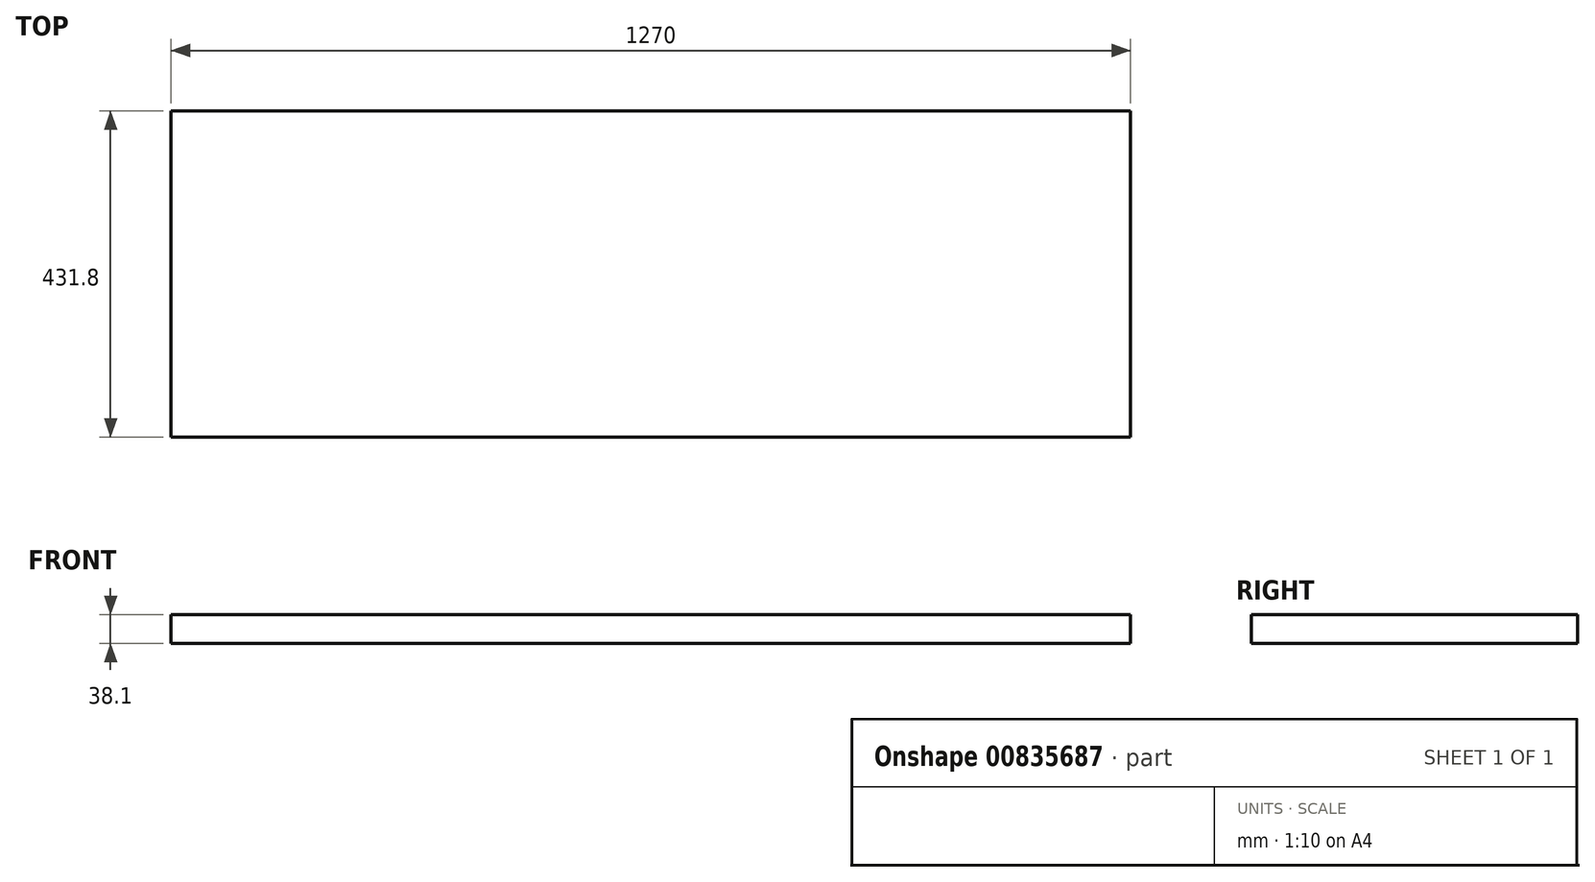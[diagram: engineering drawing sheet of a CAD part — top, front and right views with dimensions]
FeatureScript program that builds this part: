
annotation { "Feature Type Name" : "Feature", "Feature Type Description" : "" }
export const myFeature = defineFeature(function(context is Context, id is Id, definition is map)
    precondition{}
    {
        {
            var Q0;
            Q0=qCreatedBy(makeId("Top.planeOp"),FACE);
            var sketch = newSketch(context, id + "F0", { "sketchPlane" : qUnion([Q0])});
            skLineSegment(sketch, "E0.bottom", {"start": v(0, 0) * mm, "end": v(1270, 0) * mm});
            skLineSegment(sketch, "E0.top", {"start": v(0, -431.8) * mm, "end": v(1270, -431.8) * mm});
            skLineSegment(sketch, "E0.left", {"start": v(0, 0) * mm, "end": v(0, -431.8) * mm});
            skLineSegment(sketch, "E0.right", {"start": v(1270, 0) * mm, "end": v(1270, -431.8) * mm});
            skSolve(sketch);
        }
        {
            var Q0;
            Q0 = qSketchRegion(id + "F0", true);
            extrude(context, id + "F1", {"entities" : qUnion([Q0]), "depth" : 38.1 * mm, "offsetDistance" : 25.4 * mm});
        }
    });
